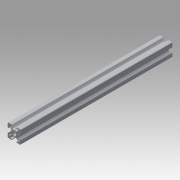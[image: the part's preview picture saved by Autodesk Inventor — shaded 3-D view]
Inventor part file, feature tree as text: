
AUTODESK INVENTOR PART (.ipt)
format: ipt  version: 2016 (Build 200138000, 138)  size: 293,888 bytes
history: native  units: in
note: dims shown in document units (in); Inventor stores cm internally (conversion verified against a paired STEP export)
features: other x3, extrude x1, sketch x1
ambient origin geometry x8: Origin, YZ Plane, XZ Plane, XY Plane, X Axis, Y Axis, Z Axis, Center Point
bodies: Solid1 (feature_tree)
feature tree (5):
  other  "Blocks"
  extrude  "Extrusion1"  [1 undecoded]
  sketch  "Sketch1"  dims[d1=0.0in]
  other  "20x20"
  other  "20x20:1"
note: 1 required parameter value undecoded (feature->parameter linkage not recoverable at this tier; creation-order binding heuristic only, values carry confidence <= 0.55)
